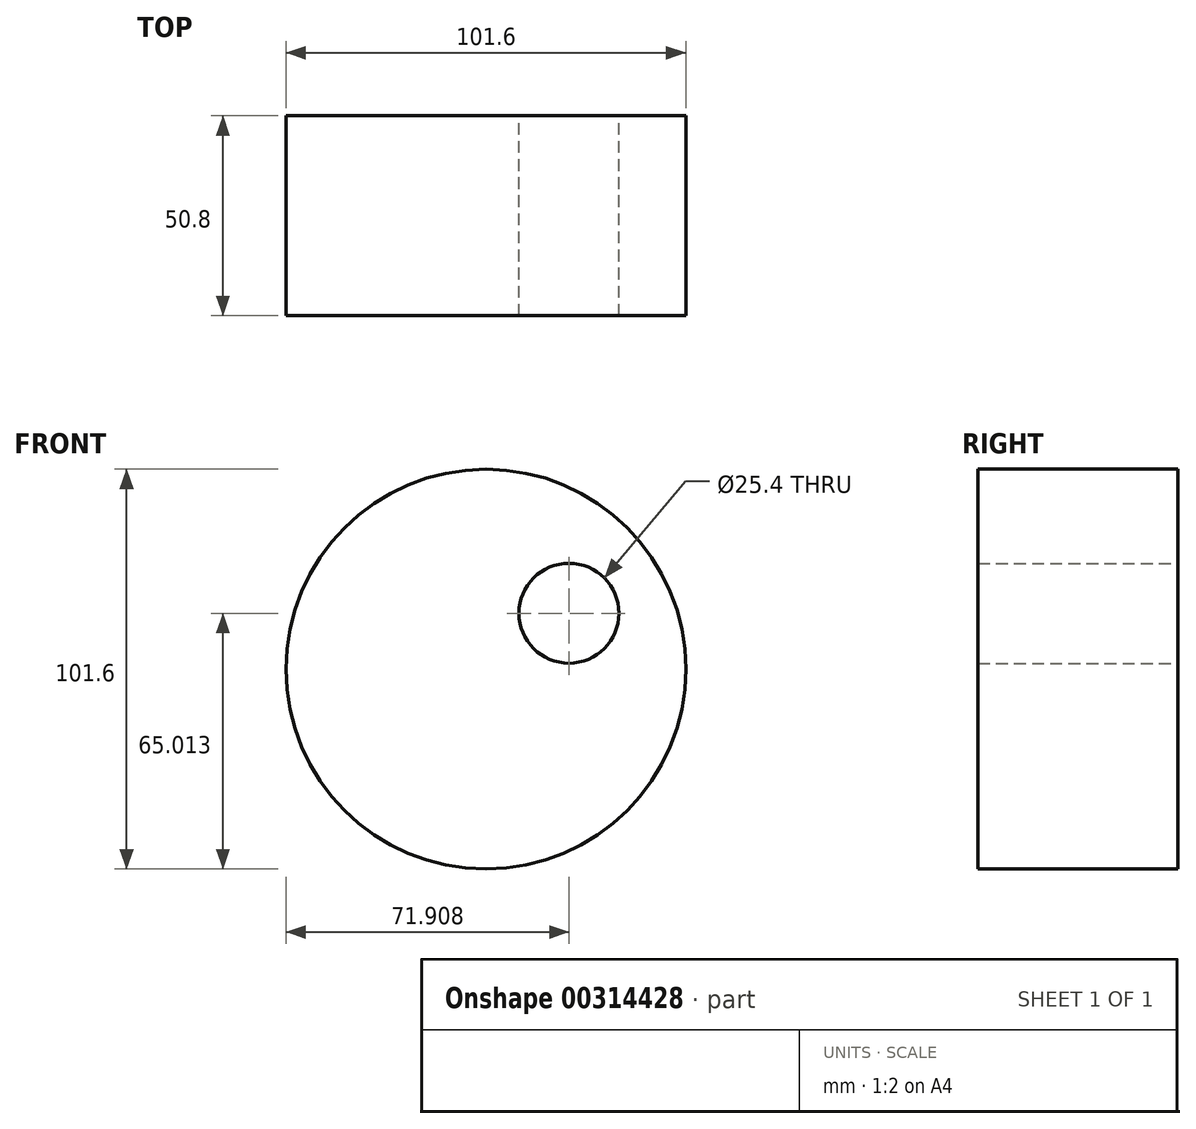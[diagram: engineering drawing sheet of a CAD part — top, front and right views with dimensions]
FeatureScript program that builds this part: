
annotation { "Feature Type Name" : "Feature", "Feature Type Description" : "" }
export const myFeature = defineFeature(function(context is Context, id is Id, definition is map)
    precondition{}
    {
        {
            var Q0;
            Q0=qCreatedBy(makeId("Front.planeOp"),FACE);
            var sketch = newSketch(context, id + "F0", { "sketchPlane" : qUnion([Q0])});
            skCircle(sketch, "E0", {"center": v(0, 0) * mm, "radius": 50.8 * mm});
            skCircle(sketch, "E1", {"center": v(21.1, 14.21) * mm, "radius": 12.7 * mm});
            skSolve(sketch);
        }
        {
            var Q0;
            Q0=makeQuery(id+"F0.imprint","IMPRINT",FACE,{"disambiguationData":[TD([[makeQuery(id+"F0.imprint","IMPRINT",EDGE,{"derivedFrom":sQuery(id+"F0.wireOp",EDGE,"E0")}),1.0]])]});
            extrude(context, id + "F1", {"entities" : qUnion([Q0]), "depth" : 50.8 * mm});
        }
    });
